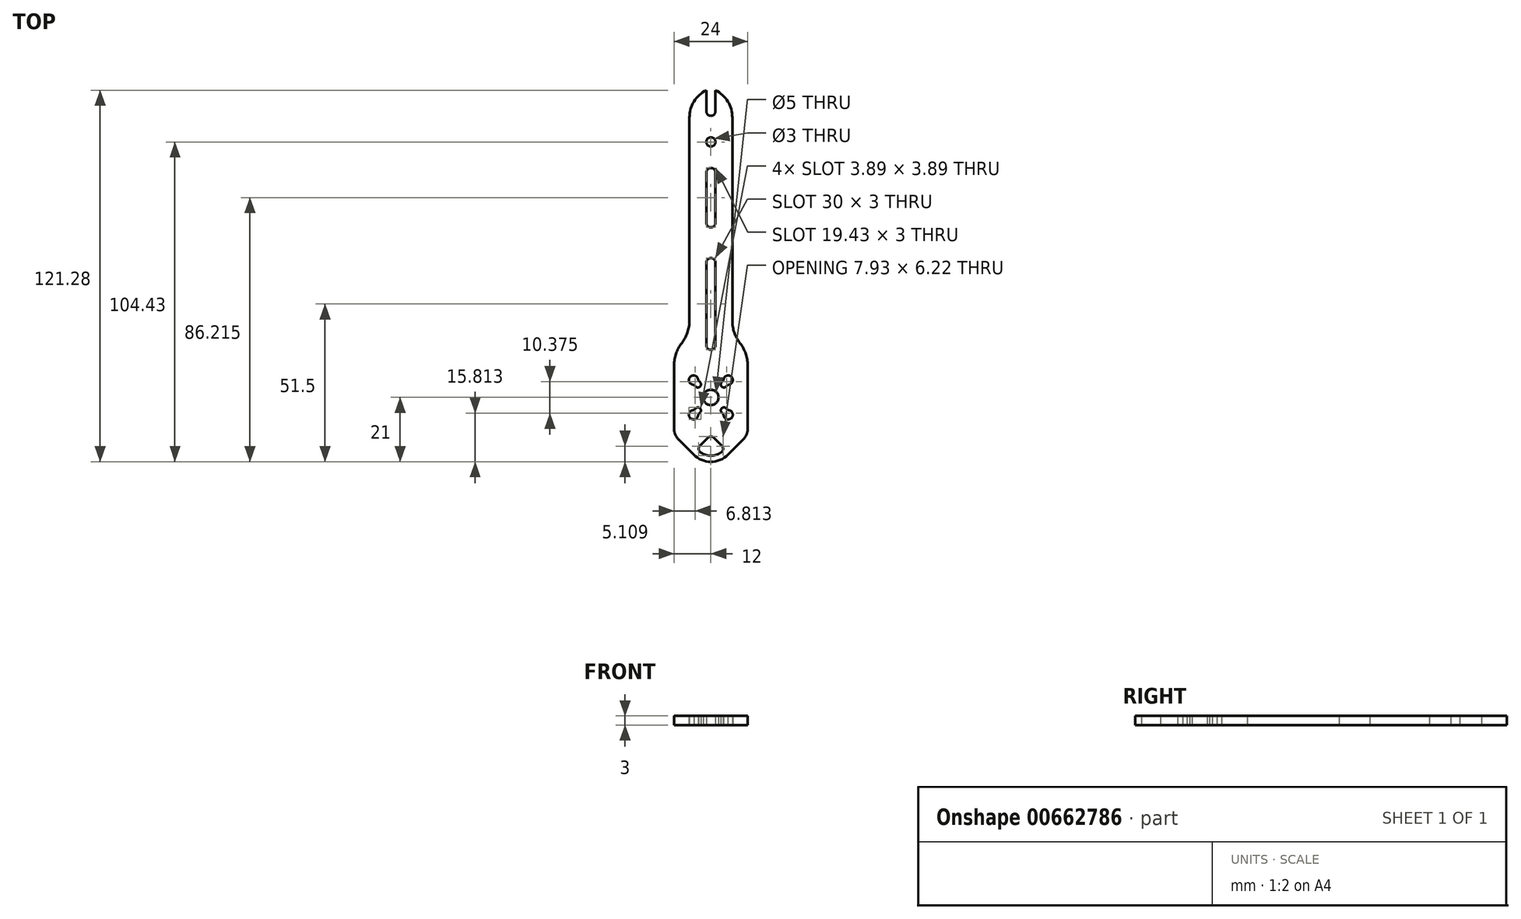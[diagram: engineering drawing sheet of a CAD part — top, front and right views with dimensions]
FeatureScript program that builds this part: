
annotation { "Feature Type Name" : "Feature", "Feature Type Description" : "" }
export const myFeature = defineFeature(function(context is Context, id is Id, definition is map)
    precondition{}
    {
        {
            var Q0;
            Q0=qCreatedBy(makeId("Top.planeOp"),FACE);
            var sketch = newSketch(context, id + "F0", { "sketchPlane" : qUnion([Q0])});
            skCircle(sketch, "E0", {"center": v(0, 0) * mm, "radius": 2.5 * mm});
            skCircle(sketch, "E1", {"center": v(0, 0) * mm, "radius": 6 * mm, "construction": true});
            skCircle(sketch, "E2", {"center": v(0, 0) * mm, "radius": 8 * mm, "construction": true});
            skLineSegment(sketch, "E3.bottom", {"start": v(4.24, 4.24) * mm, "end": v(-4.24, 4.24) * mm, "construction": true});
            skLineSegment(sketch, "E3.top", {"start": v(4.24, -4.24) * mm, "end": v(-4.24, -4.24) * mm, "construction": true});
            skLineSegment(sketch, "E3.left", {"start": v(4.24, 4.24) * mm, "end": v(4.24, -4.24) * mm, "construction": true});
            skLineSegment(sketch, "E3.right", {"start": v(-4.24, 4.24) * mm, "end": v(-4.24, -4.24) * mm, "construction": true});
            skLineSegment(sketch, "E4.bottom", {"start": v(5.66, 5.66) * mm, "end": v(-5.66, 5.66) * mm, "construction": true});
            skLineSegment(sketch, "E4.top", {"start": v(5.66, -5.66) * mm, "end": v(-5.66, -5.66) * mm, "construction": true});
            skLineSegment(sketch, "E4.left", {"start": v(5.66, 5.66) * mm, "end": v(5.66, -5.66) * mm, "construction": true});
            skLineSegment(sketch, "E4.right", {"start": v(-5.66, 5.66) * mm, "end": v(-5.66, -5.66) * mm, "construction": true});
            skCircle(sketch, "E5", {"center": v(0, 83.43) * mm, "radius": 1.5 * mm});
            skArc(sketch, "E6", {"start": v(-1.5, 93.43) * mm, "mid": v(0, 91.93) * mm, "end": v(1.5, 93.43) * mm});
            skArc(sketch, "E7", {"start": v(3.54, 4.95) * mm, "mid": v(3.54, 3.54) * mm, "end": v(4.95, 3.54) * mm});
            skArc(sketch, "E8", {"start": v(5.57, 4.16) * mm, "mid": v(6.72, 6.72) * mm, "end": v(4.16, 5.57) * mm});
            skLineSegment(sketch, "E9", {"start": v(3.54, 4.95) * mm, "end": v(4.16, 5.57) * mm});
            skLineSegment(sketch, "E10", {"start": v(4.95, 3.54) * mm, "end": v(5.57, 4.16) * mm});
            skArc(sketch, "E11.1.0", {"start": v(-4.16, 5.57) * mm, "mid": v(-6.72, 6.72) * mm, "end": v(-5.57, 4.16) * mm});
            skLineSegment(sketch, "E11.1.1", {"start": v(-3.54, 4.95) * mm, "end": v(-4.16, 5.57) * mm});
            skLineSegment(sketch, "E11.1.2", {"start": v(-4.95, 3.54) * mm, "end": v(-5.57, 4.16) * mm});
            skArc(sketch, "E11.1.3", {"start": v(-4.95, 3.54) * mm, "mid": v(-3.54, 3.54) * mm, "end": v(-3.54, 4.95) * mm});
            skArc(sketch, "E11.2.0", {"start": v(-5.57, -4.16) * mm, "mid": v(-6.72, -6.72) * mm, "end": v(-4.16, -5.57) * mm});
            skLineSegment(sketch, "E11.2.1", {"start": v(-4.95, -3.54) * mm, "end": v(-5.57, -4.16) * mm});
            skLineSegment(sketch, "E11.2.2", {"start": v(-3.54, -4.95) * mm, "end": v(-4.16, -5.57) * mm});
            skArc(sketch, "E11.2.3", {"start": v(-3.54, -4.95) * mm, "mid": v(-3.54, -3.54) * mm, "end": v(-4.95, -3.54) * mm});
            skArc(sketch, "E11.3.0", {"start": v(4.16, -5.57) * mm, "mid": v(6.72, -6.72) * mm, "end": v(5.57, -4.16) * mm});
            skLineSegment(sketch, "E11.3.1", {"start": v(3.54, -4.95) * mm, "end": v(4.16, -5.57) * mm});
            skLineSegment(sketch, "E11.3.2", {"start": v(4.95, -3.54) * mm, "end": v(5.57, -4.16) * mm});
            skArc(sketch, "E11.3.3", {"start": v(4.95, -3.54) * mm, "mid": v(3.54, -3.54) * mm, "end": v(3.54, -4.95) * mm});
            skPoint(sketch, "E12", {"position": v(-7, 25) * mm});
            skLineSegment(sketch, "E13", {"start": v(-7, 25) * mm, "end": v(-7, 91.35) * mm});
            skLineSegment(sketch, "E14", {"start": v(-1.5, 93.43) * mm, "end": v(-1.5, 100.28) * mm});
            skArc(sketch, "E15", {"start": v(-7, 91.35) * mm, "mid": v(-5.51, 96.6) * mm, "end": v(-1.5, 100.28) * mm});
            skPoint(sketch, "E16", {"position": v(-12, 10.47) * mm});
            skArc(sketch, "E17", {"start": v(-7, 25) * mm, "mid": v(-7.64, 21.16) * mm, "end": v(-9.5, 17.74) * mm});
            skLineSegment(sketch, "E18", {"start": v(-12, 10.47) * mm, "end": v(-12, -10.2) * mm});
            skArc(sketch, "E19", {"start": v(-9.5, 17.74) * mm, "mid": v(-11.36, 14.31) * mm, "end": v(-12, 10.47) * mm});
            skLineSegment(sketch, "E20", {"start": v(-10.5, -13.81) * mm, "end": v(-5.66, -18.66) * mm});
            skPoint(sketch, "E21.visualSharp", {"position": v(-12, -12.31) * mm});
            skArc(sketch, "E21.filletArc", {"start": v(-12, -10.2) * mm, "mid": v(-11.61, -12.15) * mm, "end": v(-10.5, -13.81) * mm});
            skArc(sketch, "E22.MirrorCS", {"start": v(7, 25) * mm, "mid": v(7.64, 21.16) * mm, "end": v(9.5, 17.74) * mm});
            skArc(sketch, "E23.MirrorCS", {"start": v(9.5, 17.74) * mm, "mid": v(11.36, 14.31) * mm, "end": v(12, 10.47) * mm});
            skLineSegment(sketch, "E24.MirrorCS", {"start": v(12, 10.47) * mm, "end": v(12, -10.2) * mm});
            skArc(sketch, "E25.MirrorCS", {"start": v(12, -10.2) * mm, "mid": v(11.61, -12.15) * mm, "end": v(10.5, -13.81) * mm});
            skLineSegment(sketch, "E26.MirrorCS", {"start": v(10.5, -13.81) * mm, "end": v(5.66, -18.66) * mm});
            skPoint(sketch, "E27.visualSharp", {"position": v(0, -24.31) * mm});
            skArc(sketch, "E27.filletArc", {"start": v(-5.66, -18.66) * mm, "mid": v(0, -21) * mm, "end": v(5.66, -18.66) * mm});
            skLineSegment(sketch, "E28.MirrorCS", {"start": v(7, 25) * mm, "end": v(7, 91.35) * mm});
            skLineSegment(sketch, "E29.MirrorCS", {"start": v(1.5, 93.43) * mm, "end": v(1.5, 100.28) * mm});
            skArc(sketch, "E30.MirrorCS", {"start": v(7, 91.35) * mm, "mid": v(5.51, 96.6) * mm, "end": v(1.5, 100.28) * mm});
            skArc(sketch, "E31", {"start": v(1.06, -13.22) * mm, "mid": v(0, -12.78) * mm, "end": v(-1.06, -13.22) * mm});
            skArc(sketch, "E32", {"start": v(-3.54, -15.7) * mm, "mid": v(-3.97, -16.9) * mm, "end": v(-3.3, -18.01) * mm});
            skArc(sketch, "E33.MirrorC", {"start": v(3.54, -15.7) * mm, "mid": v(3.97, -16.9) * mm, "end": v(3.3, -18.01) * mm});
            skArc(sketch, "E34", {"start": v(-3.3, -18.01) * mm, "mid": v(0, -19) * mm, "end": v(3.3, -18.01) * mm});
            skLineSegment(sketch, "E35", {"start": v(-1.06, -13.22) * mm, "end": v(-3.54, -15.7) * mm});
            skLineSegment(sketch, "E36.MirrorCS", {"start": v(1.06, -13.22) * mm, "end": v(3.54, -15.7) * mm});
            skLineSegment(sketch, "E37", {"start": v(0, 73.43) * mm, "end": v(0, 57) * mm, "construction": true});
            skLineSegment(sketch, "E38", {"start": v(0, 44) * mm, "end": v(0, 17) * mm, "construction": true});
            skArc(sketch, "E39.0.startCap", {"start": v(-1.5, 44) * mm, "mid": v(0, 45.5) * mm, "end": v(1.5, 44) * mm});
            skArc(sketch, "E39.0.endCap", {"start": v(1.5, 17) * mm, "mid": v(0, 15.5) * mm, "end": v(-1.5, 17) * mm});
            skLineSegment(sketch, "E39.0.left", {"start": v(1.5, 44) * mm, "end": v(1.5, 17) * mm});
            skLineSegment(sketch, "E39.0.right", {"start": v(-1.5, 44) * mm, "end": v(-1.5, 17) * mm});
            skArc(sketch, "E40.0.startCap", {"start": v(-1.5, 73.43) * mm, "mid": v(0, 74.93) * mm, "end": v(1.5, 73.43) * mm});
            skArc(sketch, "E40.0.endCap", {"start": v(1.5, 57) * mm, "mid": v(0, 55.5) * mm, "end": v(-1.5, 57) * mm});
            skLineSegment(sketch, "E40.0.left", {"start": v(1.5, 73.43) * mm, "end": v(1.5, 57) * mm});
            skLineSegment(sketch, "E40.0.right", {"start": v(-1.5, 73.43) * mm, "end": v(-1.5, 57) * mm});
            skSolve(sketch);
        }
        {
            var Q0;
            Q0 = qSketchRegion(id + "F0", true);
            extrude(context, id + "F1", {"entities" : qUnion([Q0]), "depth" : 3 * mm, "offsetDistance" : 25 * mm});
        }
    });
